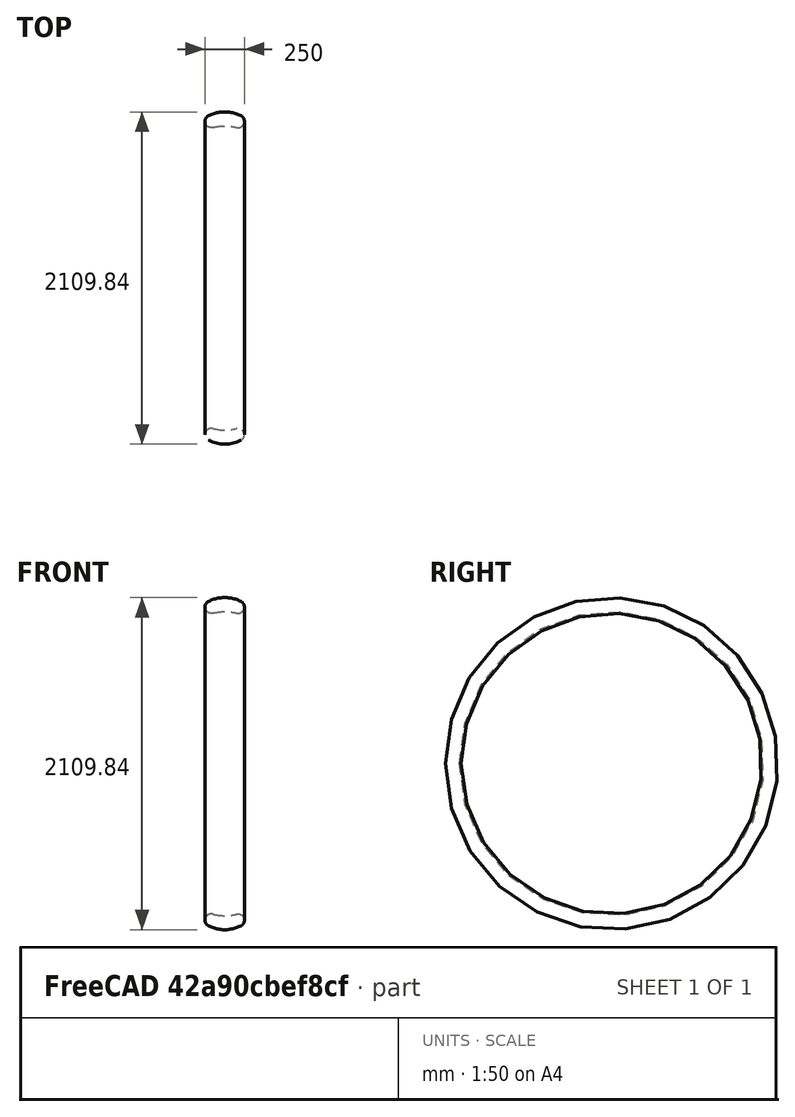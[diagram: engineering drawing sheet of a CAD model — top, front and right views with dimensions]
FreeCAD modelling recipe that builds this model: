
FCSTD DOCUMENT
Label: PR_022
objects: Sketcher::SketchObject×1, PartDesign::Revolution×1
note: 3 computed .brp shape members not serialized (recipe doc carries the construction recipe); baked Part::Feature solids carry a one-line shape summary decoded from their .brp

FEATURE [Sketcher::SketchObject] Sketch
  sketch-geometry (7):
    g0: LineSegment [constr] StartX=0 StartY=-954.92 StartZ=0 EndX=250 EndY=-954.92 EndZ=0
    g1: LineSegment [constr] StartX=250 StartY=-954.92 StartZ=0 EndX=250 EndY=-1054.92 EndZ=0
    g2: LineSegment [constr] StartX=250 StartY=-1054.92 StartZ=0 EndX=0 EndY=-1054.92 EndZ=0
    g3: ArcOfCircle CenterX=40 CenterY=-994.92 CenterZ=0 NormalX=0 NormalY=0 NormalZ=1 Radius=40 StartAngle=1.31735 EndAngle=4.25021
    g4: ArcOfCircle CenterX=210 CenterY=-994.92 CenterZ=0 NormalX=0 NormalY=0 NormalZ=1 Radius=40 StartAngle=5.17457 EndAngle=8.10742
    g5: ArcOfCircle CenterX=125 CenterY=-824.295 CenterZ=0 NormalX=0 NormalY=0 NormalZ=1 Radius=230.625 StartAngle=4.25021 EndAngle=5.17457
    g6: ArcOfCircle CenterX=125 CenterY=-666.749 CenterZ=0 NormalX=0 NormalY=0 NormalZ=1 Radius=299 StartAngle=4.45895 EndAngle=4.96583
  constraints (22):
    c: Horizontal(g0)
    c: DistanceY(g0) = -954.92
    c: Vertical(g1)
    c: Coincident(g2,g1)
    c: Horizontal(g2)
    c: PointOnObject(g2,g-2)
    c: PointOnObject(g0,g-2)
    c: Distance(g2) = 250
    c: Coincident(g1,g0)
    c: Distance(g1) = 100
    c: Radius(g3) = 40
    c: Radius(g4) = 40
    c: Tangent(g3,g-2)
    c: Tangent(g4,g1)
    c: Tangent(g4,g0)
    c: Tangent(g3,g0)
    c: Tangent(g3,g5)
    c: Tangent(g5,g4)
    c: Tangent(g5,g2)
    c: Radius(g6) = 299
    c: Tangent(g6,g4)
    c: Tangent(g3,g6)
FEATURE [PartDesign::Revolution] Revolution
  Angle = 360
  Axis = (1,0,0)
  Base = (0,0,0)
  ReferenceAxis = -> Sketch [H_Axis]
  Sketch = -> Sketch
